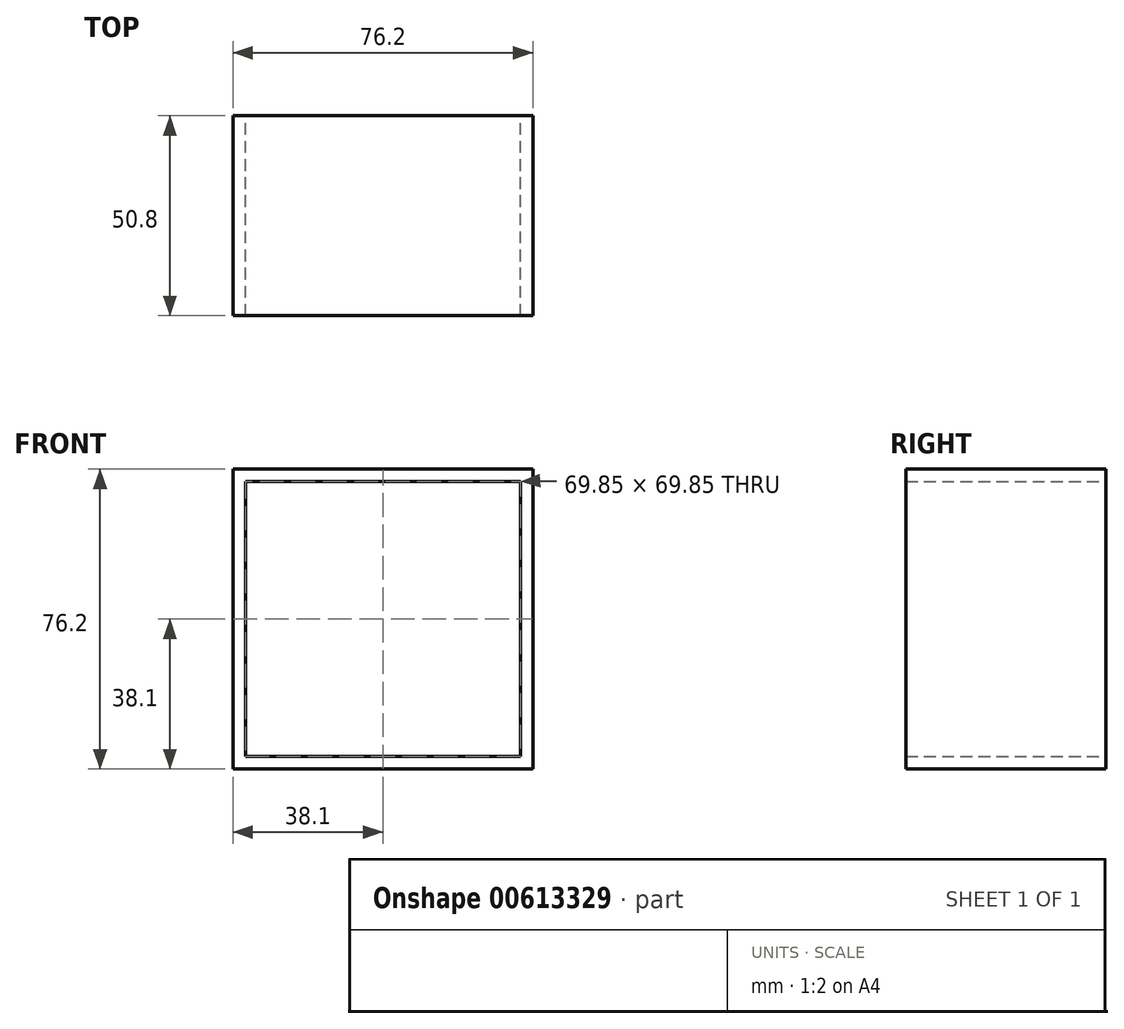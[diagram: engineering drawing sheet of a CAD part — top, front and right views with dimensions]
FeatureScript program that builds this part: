
annotation { "Feature Type Name" : "Feature", "Feature Type Description" : "" }
export const myFeature = defineFeature(function(context is Context, id is Id, definition is map)
    precondition{}
    {
        {
            var Q0;
            Q0=qCreatedBy(makeId("Front.planeOp"),FACE);
            var sketch = newSketch(context, id + "F0", { "sketchPlane" : qUnion([Q0])});
            skLineSegment(sketch, "E0.bottom", {"start": v(38.1, 38.1) * mm, "end": v(-38.1, 38.1) * mm});
            skLineSegment(sketch, "E0.top", {"start": v(38.1, -38.1) * mm, "end": v(-38.1, -38.1) * mm});
            skLineSegment(sketch, "E0.left", {"start": v(38.1, 38.1) * mm, "end": v(38.1, -38.1) * mm});
            skLineSegment(sketch, "E0.right", {"start": v(-38.1, 38.1) * mm, "end": v(-38.1, -38.1) * mm});
            skPoint(sketch, "E0.middle", {"position": v(0, 0) * mm});
            skLineSegment(sketch, "E1.0", {"start": v(34.93, 34.93) * mm, "end": v(-34.93, 34.93) * mm});
            skLineSegment(sketch, "E1.1", {"start": v(34.93, 34.93) * mm, "end": v(34.93, -34.93) * mm});
            skLineSegment(sketch, "E1.2", {"start": v(34.93, -34.93) * mm, "end": v(-34.92, -34.93) * mm});
            skLineSegment(sketch, "E1.3", {"start": v(-34.93, 34.93) * mm, "end": v(-34.92, -34.93) * mm});
            skSolve(sketch);
        }
        {
            var Q0;
            Q0 = qSketchRegion(id + "F0", true);
            extrude(context, id + "F1", {"entities" : qUnion([Q0]), "depth" : 50.8 * mm, "offsetDistance" : 25.4 * mm});
        }
    });
